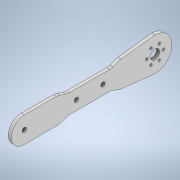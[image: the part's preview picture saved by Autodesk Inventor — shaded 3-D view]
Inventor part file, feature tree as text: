
AUTODESK INVENTOR PART (.ipt)
format: ipt  version: 2022 (Build 260153000, 153)  size: 178,688 bytes
history: native  units: mm
features: fillet x6, extrude x1, sketch x1
ambient origin geometry x8: Origin, YZ Plane, XZ Plane, XY Plane, X Axis, Y Axis, Z Axis, Center Point
bodies: Body1 (feature_tree)
feature tree (8):
  extrude  "Extrusion2"  Depth=18.0mm
  fillet  "Face Fillet1"
  fillet  "Face Fillet2"
  fillet  "Face Fillet3"
  fillet  "Face Fillet5"
  fillet  "Face Fillet6"
  fillet  "Face Fillet7"
  sketch  "Sketch1"  dims[d6=8.75mm d7=18.0mm d8=1.2mm d12=4.0mm d13=60.0mm d15=360.0deg d18=24.0mm d22=45.0mm d23=8.0mm d24=9.0mm d25=9.0mm d33=8.0mm d34=12.5mm d35=3.0mm d36=0.0mm d37=10.0mm d38=10.0mm d39=10.0mm d41=10.0mm d42=10.0mm d43=10.0mm d45=4.0mm d46=4.0mm]
